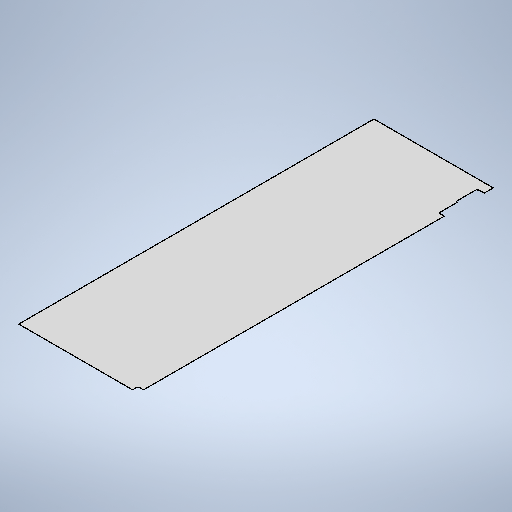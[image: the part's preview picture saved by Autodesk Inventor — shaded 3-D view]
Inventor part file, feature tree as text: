
AUTODESK INVENTOR PART (.ipt)
format: ipt  version: 2025.1 (Build 291241020, 241B)  size: 301,568 bytes
history: native  units: mm
features: other x2, sheet_metal_op x1, chamfer x1, sketch x1
ambient origin geometry x8: Origin, YZ Plane, XZ Plane, XY Plane, X Axis, Y Axis, Z Axis, Center Point
bodies: Body1 (feature_tree)
feature tree (5):
  sheet_metal_op  "Face3"
  chamfer  "Corner Round1"
  sketch  "Sketch1"  dims[d61=500.0mm d154=865.0mm d155=2575.0mm d156=2.0mm d157=40.0mm d158=15.0mm d159=290.0mm d161=40.0mm d162=2220.0mm d163=10.0mm d164=150.0mm d165=5.0mm]
  other  "Plate5"
  other  "Definition1"
